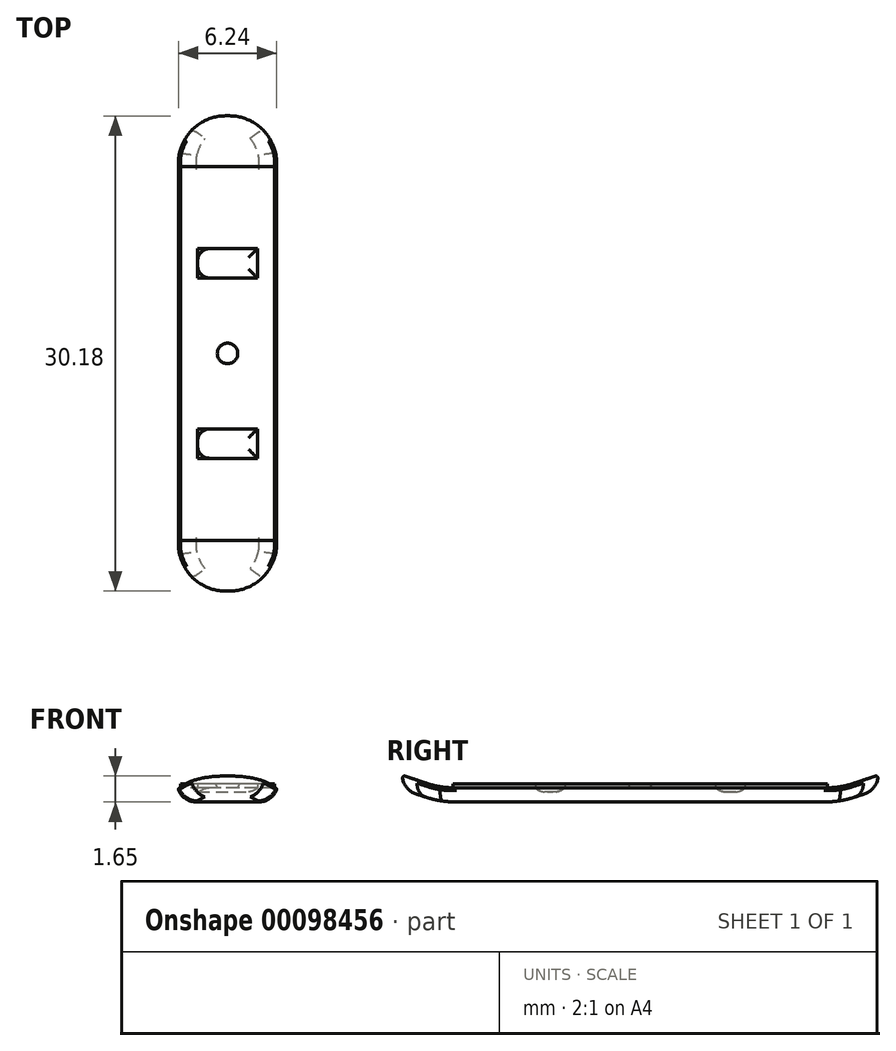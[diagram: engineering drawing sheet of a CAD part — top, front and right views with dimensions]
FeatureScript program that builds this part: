
annotation { "Feature Type Name" : "Feature", "Feature Type Description" : "" }
export const myFeature = defineFeature(function(context is Context, id is Id, definition is map)
    precondition{}
    {
        {
            var Q0;
            Q0=qCreatedBy(makeId("Right.planeOp"),FACE);
            var sketch = newSketch(context, id + "F0", { "sketchPlane" : qUnion([Q0])});
            skLineSegment(sketch, "E0", {"start": v(11.68, 0) * mm, "end": v(0, 0) * mm});
            skLineSegment(sketch, "E1", {"start": v(13.67, 0.32) * mm, "end": v(15.11, 0.8) * mm});
            skPoint(sketch, "E2.visualSharp", {"position": v(12.7, 0) * mm});
            skArc(sketch, "E2.filletArc", {"start": v(11.68, 0) * mm, "mid": v(12.69, 0.08) * mm, "end": v(13.67, 0.32) * mm});
            skLineSegment(sketch, "E3", {"start": v(0, 0.9) * mm, "end": v(12.7, 0.9) * mm});
            skLineSegment(sketch, "E4", {"start": v(12.7, 0.9) * mm, "end": v(15.11, 1.7) * mm});
            skLineSegment(sketch, "E5", {"start": v(15.11, 1.7) * mm, "end": v(15.11, 0.8) * mm});
            skLineSegment(sketch, "E6", {"start": v(0, 3.2) * mm, "end": v(0, -3.84) * mm});
            skLineSegment(sketch, "E7.MirrorCS", {"start": v(0, 0.9) * mm, "end": v(-12.7, 0.9) * mm});
            skLineSegment(sketch, "E8.MirrorCS", {"start": v(-11.68, 0) * mm, "end": v(0, 0) * mm});
            skArc(sketch, "E9.MirrorCS", {"start": v(-11.68, 0) * mm, "mid": v(-12.69, 0.08) * mm, "end": v(-13.67, 0.32) * mm});
            skLineSegment(sketch, "E10.MirrorCS", {"start": v(-12.7, 0.9) * mm, "end": v(-15.11, 1.7) * mm});
            skLineSegment(sketch, "E11.MirrorCS", {"start": v(-15.11, 1.7) * mm, "end": v(-15.11, 0.8) * mm});
            skLineSegment(sketch, "E12.MirrorCS", {"start": v(-13.67, 0.32) * mm, "end": v(-15.11, 0.8) * mm});
            skSolve(sketch);
        }
        {
            var Q0;
            {var subQ1=sQuery(id+"F0.wireOp",EDGE,"E7.MirrorCS");Q0=makeQuery(id+"F0.imprint","IMPRINT",FACE,{"disambiguationData":[TD([[makeQuery(id+"F0.imprint","IMPRINT",EDGE,{"derivedFrom":subQ1}),1.0]])]});}
            var Q1;
            {var subQ1=sQuery(id+"F0.wireOp",EDGE,"E0");Q1=makeQuery(id+"F0.imprint","IMPRINT",FACE,{"disambiguationData":[TD([[makeQuery(id+"F0.imprint","IMPRINT",EDGE,{"derivedFrom":subQ1}),-1.0]])]});}
            extrude(context, id + "F1", {"entities" : qUnion([Q0, Q1]), "depth" : 3.17 * mm});
        }
        {
            var Q0;
            Q0=makeQuery(id+"F1.opExtrude","CAP_FACE",FACE,{"disambiguationData":[OSD([sQuery(id+"F0.wireOp",EDGE,"E0"),sQuery(id+"F0.wireOp",EDGE,"E1"),sQuery(id+"F0.wireOp",EDGE,"E2.filletArc"),sQuery(id+"F0.wireOp",EDGE,"E3"),sQuery(id+"F0.wireOp",EDGE,"E4"),sQuery(id+"F0.wireOp",EDGE,"E5"),sQuery(id+"F0.wireOp",EDGE,"E7.MirrorCS"),sQuery(id+"F0.wireOp",EDGE,"E8.MirrorCS"),sQuery(id+"F0.wireOp",EDGE,"E9.MirrorCS"),sQuery(id+"F0.wireOp",EDGE,"E10.MirrorCS"),sQuery(id+"F0.wireOp",EDGE,"E11.MirrorCS"),sQuery(id+"F0.wireOp",EDGE,"E12.MirrorCS")])],"isStart":true});
            extrude(context, id + "F2", {"entities" : qUnion([Q0]), "operationType" : NewBodyOperationType.ADD, "depth" : 3.17 * mm});
        }
        {
            var Q0;
            Q0=makeQuery(id+"F1.opExtrude","CAP_EDGE",EDGE,{"disambiguationData":[OSD([sQuery(id+"F0.wireOp",EDGE,"E11.MirrorCS")])],"isStart":false});
            var Q1;
            Q1=makeQuery(id+"F2.opExtrude","CAP_EDGE",EDGE,{"disambiguationData":[OSD([sQuery(id+"F0.wireOp",EDGE,"E11.MirrorCS")])],"isStart":false});
            var Q2;
            Q2=makeQuery(id+"F1.opExtrude","CAP_EDGE",EDGE,{"disambiguationData":[OSD([sQuery(id+"F0.wireOp",EDGE,"E5")])],"isStart":false});
            var Q3;
            Q3=makeQuery(id+"F2.opExtrude","CAP_EDGE",EDGE,{"disambiguationData":[OSD([sQuery(id+"F0.wireOp",EDGE,"E5")])],"isStart":false});
            fillet(context, id + "F3", {"entities" : qUnion([Q0, Q1, Q2, Q3]), "radius" : 3.05 * mm, "tangentPropagation" : true, "allowEdgeOverflow" : false});
        }
        {
            var Q0;
            {var subQ0=sQuery(id+"F0.wireOp",EDGE,"E12.MirrorCS");Q0=makeQuery(id+"F3.opFillet","BLEND_EDGE",EDGE,{"blendedFrom":[makeQuery(id+"F2.opExtrude","CAP_EDGE",EDGE,{"disambiguationData":[OSD([sQuery(id+"F0.wireOp",EDGE,"E11.MirrorCS")])],"isStart":false}),makeQuery(id+"F2.boolean.opBoolean","MERGE",FACE,{"derivedFrom":[makeQuery(id+"F1.opExtrude","SWEPT_FACE",FACE,{"disambiguationData":[OSD([subQ0])]}),makeQuery(id+"F2.opExtrude","SWEPT_FACE",FACE,{"disambiguationData":[OSD([subQ0])]})]})],"blendedInto":[makeQuery(id+"F2.boolean.opBoolean","MERGE",FACE,{"derivedFrom":[makeQuery(id+"F1.opExtrude","SWEPT_FACE",FACE,{"disambiguationData":[OSD([subQ0])]}),makeQuery(id+"F2.opExtrude","SWEPT_FACE",FACE,{"disambiguationData":[OSD([subQ0])]})]})]});}
            var Q1;
            {var subQ0=sQuery(id+"F0.wireOp",EDGE,"E12.MirrorCS");Q1=makeQuery(id+"F3.opFillet","BLEND_EDGE",EDGE,{"blendedFrom":[makeQuery(id+"F1.opExtrude","CAP_EDGE",EDGE,{"disambiguationData":[OSD([sQuery(id+"F0.wireOp",EDGE,"E11.MirrorCS")])],"isStart":false}),makeQuery(id+"F2.boolean.opBoolean","MERGE",FACE,{"derivedFrom":[makeQuery(id+"F1.opExtrude","SWEPT_FACE",FACE,{"disambiguationData":[OSD([subQ0])]}),makeQuery(id+"F2.opExtrude","SWEPT_FACE",FACE,{"disambiguationData":[OSD([subQ0])]})]})],"blendedInto":[makeQuery(id+"F2.boolean.opBoolean","MERGE",FACE,{"derivedFrom":[makeQuery(id+"F1.opExtrude","SWEPT_FACE",FACE,{"disambiguationData":[OSD([subQ0])]}),makeQuery(id+"F2.opExtrude","SWEPT_FACE",FACE,{"disambiguationData":[OSD([subQ0])]})]})]});}
            var Q2;
            {var subQ0=sQuery(id+"F0.wireOp",EDGE,"E12.MirrorCS");var subQ1=sQuery(id+"F0.wireOp",EDGE,"E11.MirrorCS");Q2=makeQuery(id+"F2.boolean.opBoolean","MERGE",EDGE,{"derivedFrom":[makeQuery(id+"F1.opExtrude","SWEPT_EDGE",EDGE,{"disambiguationData":[OSD([subQ1,subQ0])]}),makeQuery(id+"F2.opExtrude","SWEPT_EDGE",EDGE,{"disambiguationData":[OSD([subQ1,subQ0])]})]});}
            var Q3;
            {var subQ0=sQuery(id+"F0.wireOp",EDGE,"E9.MirrorCS");Q3=makeQuery(id+"F3.opFillet","BLEND_EDGE",EDGE,{"blendedFrom":[makeQuery(id+"F1.opExtrude","CAP_EDGE",EDGE,{"disambiguationData":[OSD([sQuery(id+"F0.wireOp",EDGE,"E11.MirrorCS")])],"isStart":false}),makeQuery(id+"F2.boolean.opBoolean","MERGE",FACE,{"derivedFrom":[makeQuery(id+"F1.opExtrude","SWEPT_FACE",FACE,{"disambiguationData":[OSD([subQ0])]}),makeQuery(id+"F2.opExtrude","SWEPT_FACE",FACE,{"disambiguationData":[OSD([subQ0])]})]})],"blendedInto":[makeQuery(id+"F2.boolean.opBoolean","MERGE",FACE,{"derivedFrom":[makeQuery(id+"F1.opExtrude","SWEPT_FACE",FACE,{"disambiguationData":[OSD([subQ0])]}),makeQuery(id+"F2.opExtrude","SWEPT_FACE",FACE,{"disambiguationData":[OSD([subQ0])]})]})]});}
            var Q4;
            {var subQ0=sQuery(id+"F0.wireOp",EDGE,"E9.MirrorCS");Q4=makeQuery(id+"F3.opFillet","BLEND_EDGE",EDGE,{"blendedFrom":[makeQuery(id+"F2.opExtrude","CAP_EDGE",EDGE,{"disambiguationData":[OSD([sQuery(id+"F0.wireOp",EDGE,"E11.MirrorCS")])],"isStart":false}),makeQuery(id+"F2.boolean.opBoolean","MERGE",FACE,{"derivedFrom":[makeQuery(id+"F1.opExtrude","SWEPT_FACE",FACE,{"disambiguationData":[OSD([subQ0])]}),makeQuery(id+"F2.opExtrude","SWEPT_FACE",FACE,{"disambiguationData":[OSD([subQ0])]})]})],"blendedInto":[makeQuery(id+"F2.boolean.opBoolean","MERGE",FACE,{"derivedFrom":[makeQuery(id+"F1.opExtrude","SWEPT_FACE",FACE,{"disambiguationData":[OSD([subQ0])]}),makeQuery(id+"F2.opExtrude","SWEPT_FACE",FACE,{"disambiguationData":[OSD([subQ0])]})]})]});}
            fillet(context, id + "F4", {"entities" : qUnion([Q0, Q1, Q2, Q3, Q4]), "radius" : 1.27 * mm, "tangentPropagation" : true, "allowEdgeOverflow" : false});
        }
        {
            var Q0;
            {var subQ0=sQuery(id+"F0.wireOp",EDGE,"E4");var subQ1=sQuery(id+"F0.wireOp",EDGE,"E3");Q0=makeQuery(id+"F2.boolean.opBoolean","MERGE",EDGE,{"derivedFrom":[makeQuery(id+"F1.opExtrude","SWEPT_EDGE",EDGE,{"disambiguationData":[OSD([subQ1,subQ0])]}),makeQuery(id+"F2.opExtrude","SWEPT_EDGE",EDGE,{"disambiguationData":[OSD([subQ1,subQ0])]})]});}
            var Q1;
            {var subQ0=sQuery(id+"F0.wireOp",EDGE,"E10.MirrorCS");var subQ1=sQuery(id+"F0.wireOp",EDGE,"E7.MirrorCS");Q1=makeQuery(id+"F2.boolean.opBoolean","MERGE",EDGE,{"derivedFrom":[makeQuery(id+"F1.opExtrude","SWEPT_EDGE",EDGE,{"disambiguationData":[OSD([subQ1,subQ0])]}),makeQuery(id+"F2.opExtrude","SWEPT_EDGE",EDGE,{"disambiguationData":[OSD([subQ1,subQ0])]})]});}
            fillet(context, id + "F5", {"entities" : qUnion([Q0, Q1]), "radius" : 5.08 * mm, "tangentPropagation" : true, "allowEdgeOverflow" : false});
        }
        {
            var Q0;
            {var subQ0=sQuery(id+"F0.wireOp",EDGE,"E7.MirrorCS");var subQ1=sQuery(id+"F0.wireOp",EDGE,"E3");Q0=makeQuery(id+"F4.opFillet","BLEND_EDGE",EDGE,{"disambiguationData":[OD(1.0)],"blendedFrom":[makeQuery(id+"F1.opExtrude","CAP_EDGE",EDGE,{"disambiguationData":[OSD([sQuery(id+"F0.wireOp",EDGE,"E2.filletArc")])],"isStart":false}),makeQuery(id+"F2.boolean.opBoolean","MERGE",FACE,{"derivedFrom":[makeQuery(id+"F1.opExtrude","SWEPT_FACE",FACE,{"disambiguationData":[OSD([subQ1,subQ0])]}),makeQuery(id+"F2.opExtrude","SWEPT_FACE",FACE,{"disambiguationData":[OSD([subQ1,subQ0])]})]})],"blendedInto":[makeQuery(id+"F2.boolean.opBoolean","MERGE",FACE,{"derivedFrom":[makeQuery(id+"F1.opExtrude","SWEPT_FACE",FACE,{"disambiguationData":[OSD([subQ1,subQ0])]}),makeQuery(id+"F2.opExtrude","SWEPT_FACE",FACE,{"disambiguationData":[OSD([subQ1,subQ0])]})]})]});}
            var Q1;
            {var subQ0=sQuery(id+"F0.wireOp",EDGE,"E7.MirrorCS");var subQ1=sQuery(id+"F0.wireOp",EDGE,"E3");Q1=makeQuery(id+"F4.opFillet","BLEND_EDGE",EDGE,{"disambiguationData":[OD(1.0)],"blendedFrom":[makeQuery(id+"F2.opExtrude","CAP_EDGE",EDGE,{"disambiguationData":[OSD([sQuery(id+"F0.wireOp",EDGE,"E9.MirrorCS")])],"isStart":false}),makeQuery(id+"F2.boolean.opBoolean","MERGE",FACE,{"derivedFrom":[makeQuery(id+"F1.opExtrude","SWEPT_FACE",FACE,{"disambiguationData":[OSD([subQ1,subQ0])]}),makeQuery(id+"F2.opExtrude","SWEPT_FACE",FACE,{"disambiguationData":[OSD([subQ1,subQ0])]})]})],"blendedInto":[makeQuery(id+"F2.boolean.opBoolean","MERGE",FACE,{"derivedFrom":[makeQuery(id+"F1.opExtrude","SWEPT_FACE",FACE,{"disambiguationData":[OSD([subQ1,subQ0])]}),makeQuery(id+"F2.opExtrude","SWEPT_FACE",FACE,{"disambiguationData":[OSD([subQ1,subQ0])]})]})]});}
            var Q2;
            {var subQ0=sQuery(id+"F0.wireOp",EDGE,"E7.MirrorCS");var subQ1=sQuery(id+"F0.wireOp",EDGE,"E3");Q2=makeQuery(id+"F4.opFillet","BLEND_EDGE",EDGE,{"disambiguationData":[OD(0.0)],"blendedFrom":[makeQuery(id+"F2.opExtrude","CAP_EDGE",EDGE,{"disambiguationData":[OSD([sQuery(id+"F0.wireOp",EDGE,"E9.MirrorCS")])],"isStart":false}),makeQuery(id+"F2.boolean.opBoolean","MERGE",FACE,{"derivedFrom":[makeQuery(id+"F1.opExtrude","SWEPT_FACE",FACE,{"disambiguationData":[OSD([subQ1,subQ0])]}),makeQuery(id+"F2.opExtrude","SWEPT_FACE",FACE,{"disambiguationData":[OSD([subQ1,subQ0])]})]})],"blendedInto":[makeQuery(id+"F2.boolean.opBoolean","MERGE",FACE,{"derivedFrom":[makeQuery(id+"F1.opExtrude","SWEPT_FACE",FACE,{"disambiguationData":[OSD([subQ1,subQ0])]}),makeQuery(id+"F2.opExtrude","SWEPT_FACE",FACE,{"disambiguationData":[OSD([subQ1,subQ0])]})]})]});}
            var Q3;
            {var subQ0=sQuery(id+"F0.wireOp",EDGE,"E9.MirrorCS");var subQ1=sQuery(id+"F0.wireOp",EDGE,"E10.MirrorCS");var subQ2=sQuery(id+"F0.wireOp",EDGE,"E7.MirrorCS");Q3=makeQuery(id+"F5.opFillet","BLEND_EDGE",EDGE,{"blendedFrom":[makeQuery(id+"F2.boolean.opBoolean","MERGE",EDGE,{"derivedFrom":[makeQuery(id+"F1.opExtrude","SWEPT_EDGE",EDGE,{"disambiguationData":[OSD([subQ2,subQ1])]}),makeQuery(id+"F2.opExtrude","SWEPT_EDGE",EDGE,{"disambiguationData":[OSD([subQ2,subQ1])]})]}),makeQuery(id+"F4.opFillet","BLEND_FACE",FACE,{"disambiguationData":[OSD([subQ0]),TDD([makeQuery(id+"F2.opExtrude","CAP_EDGE",EDGE,{"disambiguationData":[OSD([subQ0])],"isStart":false})]),OD(1.0)]})],"blendedInto":[makeQuery(id+"F4.opFillet","BLEND_FACE",FACE,{"disambiguationData":[OSD([subQ0]),TDD([makeQuery(id+"F2.opExtrude","CAP_EDGE",EDGE,{"disambiguationData":[OSD([subQ0])],"isStart":false})]),OD(1.0)]})]});}
            var Q4;
            {var subQ0=sQuery(id+"F0.wireOp",EDGE,"E9.MirrorCS");var subQ1=sQuery(id+"F0.wireOp",EDGE,"E11.MirrorCS");var subQ2=sQuery(id+"F0.wireOp",EDGE,"E10.MirrorCS");var subQ3=sQuery(id+"F0.wireOp",EDGE,"E7.MirrorCS");Q4=makeQuery(id+"F5.opFillet","BLEND_EDGE",EDGE,{"blendedFrom":[makeQuery(id+"F2.boolean.opBoolean","MERGE",EDGE,{"derivedFrom":[makeQuery(id+"F1.opExtrude","SWEPT_EDGE",EDGE,{"disambiguationData":[OSD([subQ3,subQ2])]}),makeQuery(id+"F2.opExtrude","SWEPT_EDGE",EDGE,{"disambiguationData":[OSD([subQ3,subQ2])]})]}),makeQuery(id+"F4.opFillet","BLEND_FACE",FACE,{"disambiguationData":[OSD([subQ0,subQ1]),TDD([makeQuery(id+"F3.opFillet","BLEND_EDGE",EDGE,{"blendedFrom":[makeQuery(id+"F2.opExtrude","CAP_EDGE",EDGE,{"disambiguationData":[OSD([subQ1])],"isStart":false}),makeQuery(id+"F2.boolean.opBoolean","MERGE",FACE,{"derivedFrom":[makeQuery(id+"F1.opExtrude","SWEPT_FACE",FACE,{"disambiguationData":[OSD([subQ0])]}),makeQuery(id+"F2.opExtrude","SWEPT_FACE",FACE,{"disambiguationData":[OSD([subQ0])]})]})],"blendedInto":[makeQuery(id+"F2.boolean.opBoolean","MERGE",FACE,{"derivedFrom":[makeQuery(id+"F1.opExtrude","SWEPT_FACE",FACE,{"disambiguationData":[OSD([subQ0])]}),makeQuery(id+"F2.opExtrude","SWEPT_FACE",FACE,{"disambiguationData":[OSD([subQ0])]})]})]})])]})],"blendedInto":[makeQuery(id+"F4.opFillet","BLEND_FACE",FACE,{"disambiguationData":[OSD([subQ0,subQ1]),TDD([makeQuery(id+"F3.opFillet","BLEND_EDGE",EDGE,{"blendedFrom":[makeQuery(id+"F2.opExtrude","CAP_EDGE",EDGE,{"disambiguationData":[OSD([subQ1])],"isStart":false}),makeQuery(id+"F2.boolean.opBoolean","MERGE",FACE,{"derivedFrom":[makeQuery(id+"F1.opExtrude","SWEPT_FACE",FACE,{"disambiguationData":[OSD([subQ0])]}),makeQuery(id+"F2.opExtrude","SWEPT_FACE",FACE,{"disambiguationData":[OSD([subQ0])]})]})],"blendedInto":[makeQuery(id+"F2.boolean.opBoolean","MERGE",FACE,{"derivedFrom":[makeQuery(id+"F1.opExtrude","SWEPT_FACE",FACE,{"disambiguationData":[OSD([subQ0])]}),makeQuery(id+"F2.opExtrude","SWEPT_FACE",FACE,{"disambiguationData":[OSD([subQ0])]})]})]})])]})]});}
            var Q5;
            {var subQ0=sQuery(id+"F0.wireOp",EDGE,"E12.MirrorCS");var subQ1=sQuery(id+"F0.wireOp",EDGE,"E11.MirrorCS");var subQ2=sQuery(id+"F0.wireOp",EDGE,"E10.MirrorCS");var subQ3=sQuery(id+"F0.wireOp",EDGE,"E7.MirrorCS");Q5=makeQuery(id+"F5.opFillet","BLEND_EDGE",EDGE,{"blendedFrom":[makeQuery(id+"F2.boolean.opBoolean","MERGE",EDGE,{"derivedFrom":[makeQuery(id+"F1.opExtrude","SWEPT_EDGE",EDGE,{"disambiguationData":[OSD([subQ3,subQ2])]}),makeQuery(id+"F2.opExtrude","SWEPT_EDGE",EDGE,{"disambiguationData":[OSD([subQ3,subQ2])]})]}),makeQuery(id+"F4.opFillet","BLEND_FACE",FACE,{"disambiguationData":[OSD([subQ1,subQ0]),TDD([makeQuery(id+"F3.opFillet","BLEND_EDGE",EDGE,{"blendedFrom":[makeQuery(id+"F2.opExtrude","CAP_EDGE",EDGE,{"disambiguationData":[OSD([subQ1])],"isStart":false}),makeQuery(id+"F2.boolean.opBoolean","MERGE",FACE,{"derivedFrom":[makeQuery(id+"F1.opExtrude","SWEPT_FACE",FACE,{"disambiguationData":[OSD([subQ0])]}),makeQuery(id+"F2.opExtrude","SWEPT_FACE",FACE,{"disambiguationData":[OSD([subQ0])]})]})],"blendedInto":[makeQuery(id+"F2.boolean.opBoolean","MERGE",FACE,{"derivedFrom":[makeQuery(id+"F1.opExtrude","SWEPT_FACE",FACE,{"disambiguationData":[OSD([subQ0])]}),makeQuery(id+"F2.opExtrude","SWEPT_FACE",FACE,{"disambiguationData":[OSD([subQ0])]})]})]})]),OD(0.0)]})],"blendedInto":[makeQuery(id+"F4.opFillet","BLEND_FACE",FACE,{"disambiguationData":[OSD([subQ1,subQ0]),TDD([makeQuery(id+"F3.opFillet","BLEND_EDGE",EDGE,{"blendedFrom":[makeQuery(id+"F2.opExtrude","CAP_EDGE",EDGE,{"disambiguationData":[OSD([subQ1])],"isStart":false}),makeQuery(id+"F2.boolean.opBoolean","MERGE",FACE,{"derivedFrom":[makeQuery(id+"F1.opExtrude","SWEPT_FACE",FACE,{"disambiguationData":[OSD([subQ0])]}),makeQuery(id+"F2.opExtrude","SWEPT_FACE",FACE,{"disambiguationData":[OSD([subQ0])]})]})],"blendedInto":[makeQuery(id+"F2.boolean.opBoolean","MERGE",FACE,{"derivedFrom":[makeQuery(id+"F1.opExtrude","SWEPT_FACE",FACE,{"disambiguationData":[OSD([subQ0])]}),makeQuery(id+"F2.opExtrude","SWEPT_FACE",FACE,{"disambiguationData":[OSD([subQ0])]})]})]})]),OD(0.0)]})]});}
            var Q6;
            {var subQ0=sQuery(id+"F0.wireOp",EDGE,"E10.MirrorCS");var subQ1=sQuery(id+"F0.wireOp",EDGE,"E12.MirrorCS");Q6=makeQuery(id+"F4.opFillet","BLEND_EDGE",EDGE,{"disambiguationData":[OD(0.0)],"blendedFrom":[makeQuery(id+"F3.opFillet","BLEND_EDGE",EDGE,{"blendedFrom":[makeQuery(id+"F2.opExtrude","CAP_EDGE",EDGE,{"disambiguationData":[OSD([sQuery(id+"F0.wireOp",EDGE,"E11.MirrorCS")])],"isStart":false}),makeQuery(id+"F2.boolean.opBoolean","MERGE",FACE,{"derivedFrom":[makeQuery(id+"F1.opExtrude","SWEPT_FACE",FACE,{"disambiguationData":[OSD([subQ1])]}),makeQuery(id+"F2.opExtrude","SWEPT_FACE",FACE,{"disambiguationData":[OSD([subQ1])]})]})],"blendedInto":[makeQuery(id+"F2.boolean.opBoolean","MERGE",FACE,{"derivedFrom":[makeQuery(id+"F1.opExtrude","SWEPT_FACE",FACE,{"disambiguationData":[OSD([subQ1])]}),makeQuery(id+"F2.opExtrude","SWEPT_FACE",FACE,{"disambiguationData":[OSD([subQ1])]})]})]}),makeQuery(id+"F2.boolean.opBoolean","MERGE",FACE,{"derivedFrom":[makeQuery(id+"F1.opExtrude","SWEPT_FACE",FACE,{"disambiguationData":[OSD([subQ0])]}),makeQuery(id+"F2.opExtrude","SWEPT_FACE",FACE,{"disambiguationData":[OSD([subQ0])]})]})],"blendedInto":[makeQuery(id+"F2.boolean.opBoolean","MERGE",FACE,{"derivedFrom":[makeQuery(id+"F1.opExtrude","SWEPT_FACE",FACE,{"disambiguationData":[OSD([subQ0])]}),makeQuery(id+"F2.opExtrude","SWEPT_FACE",FACE,{"disambiguationData":[OSD([subQ0])]})]})]});}
            var Q7;
            {var subQ0=sQuery(id+"F0.wireOp",EDGE,"E10.MirrorCS");var subQ1=sQuery(id+"F0.wireOp",EDGE,"E12.MirrorCS");Q7=makeQuery(id+"F4.opFillet","BLEND_EDGE",EDGE,{"disambiguationData":[OD(1.0)],"blendedFrom":[makeQuery(id+"F3.opFillet","BLEND_EDGE",EDGE,{"blendedFrom":[makeQuery(id+"F2.opExtrude","CAP_EDGE",EDGE,{"disambiguationData":[OSD([sQuery(id+"F0.wireOp",EDGE,"E11.MirrorCS")])],"isStart":false}),makeQuery(id+"F2.boolean.opBoolean","MERGE",FACE,{"derivedFrom":[makeQuery(id+"F1.opExtrude","SWEPT_FACE",FACE,{"disambiguationData":[OSD([subQ1])]}),makeQuery(id+"F2.opExtrude","SWEPT_FACE",FACE,{"disambiguationData":[OSD([subQ1])]})]})],"blendedInto":[makeQuery(id+"F2.boolean.opBoolean","MERGE",FACE,{"derivedFrom":[makeQuery(id+"F1.opExtrude","SWEPT_FACE",FACE,{"disambiguationData":[OSD([subQ1])]}),makeQuery(id+"F2.opExtrude","SWEPT_FACE",FACE,{"disambiguationData":[OSD([subQ1])]})]})]}),makeQuery(id+"F2.boolean.opBoolean","MERGE",FACE,{"derivedFrom":[makeQuery(id+"F1.opExtrude","SWEPT_FACE",FACE,{"disambiguationData":[OSD([subQ0])]}),makeQuery(id+"F2.opExtrude","SWEPT_FACE",FACE,{"disambiguationData":[OSD([subQ0])]})]})],"blendedInto":[makeQuery(id+"F2.boolean.opBoolean","MERGE",FACE,{"derivedFrom":[makeQuery(id+"F1.opExtrude","SWEPT_FACE",FACE,{"disambiguationData":[OSD([subQ0])]}),makeQuery(id+"F2.opExtrude","SWEPT_FACE",FACE,{"disambiguationData":[OSD([subQ0])]})]})]});}
            var Q8;
            {var subQ0=sQuery(id+"F0.wireOp",EDGE,"E10.MirrorCS");var subQ1=sQuery(id+"F0.wireOp",EDGE,"E12.MirrorCS");var subQ2=sQuery(id+"F0.wireOp",EDGE,"E11.MirrorCS");Q8=makeQuery(id+"F4.opFillet","BLEND_EDGE",EDGE,{"blendedFrom":[makeQuery(id+"F2.boolean.opBoolean","MERGE",EDGE,{"derivedFrom":[makeQuery(id+"F1.opExtrude","SWEPT_EDGE",EDGE,{"disambiguationData":[OSD([subQ2,subQ1])]}),makeQuery(id+"F2.opExtrude","SWEPT_EDGE",EDGE,{"disambiguationData":[OSD([subQ2,subQ1])]})]}),makeQuery(id+"F2.boolean.opBoolean","MERGE",FACE,{"derivedFrom":[makeQuery(id+"F1.opExtrude","SWEPT_FACE",FACE,{"disambiguationData":[OSD([subQ0])]}),makeQuery(id+"F2.opExtrude","SWEPT_FACE",FACE,{"disambiguationData":[OSD([subQ0])]})]})],"blendedInto":[makeQuery(id+"F2.boolean.opBoolean","MERGE",FACE,{"derivedFrom":[makeQuery(id+"F1.opExtrude","SWEPT_FACE",FACE,{"disambiguationData":[OSD([subQ0])]}),makeQuery(id+"F2.opExtrude","SWEPT_FACE",FACE,{"disambiguationData":[OSD([subQ0])]})]})]});}
            var Q9;
            {var subQ0=sQuery(id+"F0.wireOp",EDGE,"E10.MirrorCS");var subQ1=sQuery(id+"F0.wireOp",EDGE,"E12.MirrorCS");Q9=makeQuery(id+"F4.opFillet","BLEND_EDGE",EDGE,{"blendedFrom":[makeQuery(id+"F3.opFillet","BLEND_EDGE",EDGE,{"blendedFrom":[makeQuery(id+"F1.opExtrude","CAP_EDGE",EDGE,{"disambiguationData":[OSD([sQuery(id+"F0.wireOp",EDGE,"E11.MirrorCS")])],"isStart":false}),makeQuery(id+"F2.boolean.opBoolean","MERGE",FACE,{"derivedFrom":[makeQuery(id+"F1.opExtrude","SWEPT_FACE",FACE,{"disambiguationData":[OSD([subQ1])]}),makeQuery(id+"F2.opExtrude","SWEPT_FACE",FACE,{"disambiguationData":[OSD([subQ1])]})]})],"blendedInto":[makeQuery(id+"F2.boolean.opBoolean","MERGE",FACE,{"derivedFrom":[makeQuery(id+"F1.opExtrude","SWEPT_FACE",FACE,{"disambiguationData":[OSD([subQ1])]}),makeQuery(id+"F2.opExtrude","SWEPT_FACE",FACE,{"disambiguationData":[OSD([subQ1])]})]})]}),makeQuery(id+"F2.boolean.opBoolean","MERGE",FACE,{"derivedFrom":[makeQuery(id+"F1.opExtrude","SWEPT_FACE",FACE,{"disambiguationData":[OSD([subQ0])]}),makeQuery(id+"F2.opExtrude","SWEPT_FACE",FACE,{"disambiguationData":[OSD([subQ0])]})]})],"blendedInto":[makeQuery(id+"F2.boolean.opBoolean","MERGE",FACE,{"derivedFrom":[makeQuery(id+"F1.opExtrude","SWEPT_FACE",FACE,{"disambiguationData":[OSD([subQ0])]}),makeQuery(id+"F2.opExtrude","SWEPT_FACE",FACE,{"disambiguationData":[OSD([subQ0])]})]})]});}
            var Q10;
            {var subQ0=sQuery(id+"F0.wireOp",EDGE,"E10.MirrorCS");var subQ1=sQuery(id+"F0.wireOp",EDGE,"E9.MirrorCS");Q10=makeQuery(id+"F4.opFillet","BLEND_EDGE",EDGE,{"blendedFrom":[makeQuery(id+"F3.opFillet","BLEND_EDGE",EDGE,{"blendedFrom":[makeQuery(id+"F1.opExtrude","CAP_EDGE",EDGE,{"disambiguationData":[OSD([sQuery(id+"F0.wireOp",EDGE,"E11.MirrorCS")])],"isStart":false}),makeQuery(id+"F2.boolean.opBoolean","MERGE",FACE,{"derivedFrom":[makeQuery(id+"F1.opExtrude","SWEPT_FACE",FACE,{"disambiguationData":[OSD([subQ1])]}),makeQuery(id+"F2.opExtrude","SWEPT_FACE",FACE,{"disambiguationData":[OSD([subQ1])]})]})],"blendedInto":[makeQuery(id+"F2.boolean.opBoolean","MERGE",FACE,{"derivedFrom":[makeQuery(id+"F1.opExtrude","SWEPT_FACE",FACE,{"disambiguationData":[OSD([subQ1])]}),makeQuery(id+"F2.opExtrude","SWEPT_FACE",FACE,{"disambiguationData":[OSD([subQ1])]})]})]}),makeQuery(id+"F2.boolean.opBoolean","MERGE",FACE,{"derivedFrom":[makeQuery(id+"F1.opExtrude","SWEPT_FACE",FACE,{"disambiguationData":[OSD([subQ0])]}),makeQuery(id+"F2.opExtrude","SWEPT_FACE",FACE,{"disambiguationData":[OSD([subQ0])]})]})],"blendedInto":[makeQuery(id+"F2.boolean.opBoolean","MERGE",FACE,{"derivedFrom":[makeQuery(id+"F1.opExtrude","SWEPT_FACE",FACE,{"disambiguationData":[OSD([subQ0])]}),makeQuery(id+"F2.opExtrude","SWEPT_FACE",FACE,{"disambiguationData":[OSD([subQ0])]})]})]});}
            var Q11;
            {var subQ0=sQuery(id+"F0.wireOp",EDGE,"E9.MirrorCS");var subQ1=sQuery(id+"F0.wireOp",EDGE,"E11.MirrorCS");var subQ2=sQuery(id+"F0.wireOp",EDGE,"E10.MirrorCS");var subQ3=sQuery(id+"F0.wireOp",EDGE,"E7.MirrorCS");Q11=makeQuery(id+"F5.opFillet","BLEND_EDGE",EDGE,{"blendedFrom":[makeQuery(id+"F2.boolean.opBoolean","MERGE",EDGE,{"derivedFrom":[makeQuery(id+"F1.opExtrude","SWEPT_EDGE",EDGE,{"disambiguationData":[OSD([subQ3,subQ2])]}),makeQuery(id+"F2.opExtrude","SWEPT_EDGE",EDGE,{"disambiguationData":[OSD([subQ3,subQ2])]})]}),makeQuery(id+"F4.opFillet","BLEND_FACE",FACE,{"disambiguationData":[OSD([subQ0,subQ1]),TDD([makeQuery(id+"F3.opFillet","BLEND_EDGE",EDGE,{"blendedFrom":[makeQuery(id+"F1.opExtrude","CAP_EDGE",EDGE,{"disambiguationData":[OSD([subQ1])],"isStart":false}),makeQuery(id+"F2.boolean.opBoolean","MERGE",FACE,{"derivedFrom":[makeQuery(id+"F1.opExtrude","SWEPT_FACE",FACE,{"disambiguationData":[OSD([subQ0])]}),makeQuery(id+"F2.opExtrude","SWEPT_FACE",FACE,{"disambiguationData":[OSD([subQ0])]})]})],"blendedInto":[makeQuery(id+"F2.boolean.opBoolean","MERGE",FACE,{"derivedFrom":[makeQuery(id+"F1.opExtrude","SWEPT_FACE",FACE,{"disambiguationData":[OSD([subQ0])]}),makeQuery(id+"F2.opExtrude","SWEPT_FACE",FACE,{"disambiguationData":[OSD([subQ0])]})]})]})]),OD(0.0)]})],"blendedInto":[makeQuery(id+"F4.opFillet","BLEND_FACE",FACE,{"disambiguationData":[OSD([subQ0,subQ1]),TDD([makeQuery(id+"F3.opFillet","BLEND_EDGE",EDGE,{"blendedFrom":[makeQuery(id+"F1.opExtrude","CAP_EDGE",EDGE,{"disambiguationData":[OSD([subQ1])],"isStart":false}),makeQuery(id+"F2.boolean.opBoolean","MERGE",FACE,{"derivedFrom":[makeQuery(id+"F1.opExtrude","SWEPT_FACE",FACE,{"disambiguationData":[OSD([subQ0])]}),makeQuery(id+"F2.opExtrude","SWEPT_FACE",FACE,{"disambiguationData":[OSD([subQ0])]})]})],"blendedInto":[makeQuery(id+"F2.boolean.opBoolean","MERGE",FACE,{"derivedFrom":[makeQuery(id+"F1.opExtrude","SWEPT_FACE",FACE,{"disambiguationData":[OSD([subQ0])]}),makeQuery(id+"F2.opExtrude","SWEPT_FACE",FACE,{"disambiguationData":[OSD([subQ0])]})]})]})]),OD(0.0)]})]});}
            var Q12;
            {var subQ0=sQuery(id+"F0.wireOp",EDGE,"E9.MirrorCS");var subQ1=sQuery(id+"F0.wireOp",EDGE,"E11.MirrorCS");var subQ2=sQuery(id+"F0.wireOp",EDGE,"E10.MirrorCS");var subQ3=sQuery(id+"F0.wireOp",EDGE,"E7.MirrorCS");Q12=makeQuery(id+"F5.opFillet","BLEND_EDGE",EDGE,{"blendedFrom":[makeQuery(id+"F2.boolean.opBoolean","MERGE",EDGE,{"derivedFrom":[makeQuery(id+"F1.opExtrude","SWEPT_EDGE",EDGE,{"disambiguationData":[OSD([subQ3,subQ2])]}),makeQuery(id+"F2.opExtrude","SWEPT_EDGE",EDGE,{"disambiguationData":[OSD([subQ3,subQ2])]})]}),makeQuery(id+"F4.opFillet","BLEND_FACE",FACE,{"disambiguationData":[OSD([subQ0,subQ1]),TDD([makeQuery(id+"F3.opFillet","BLEND_EDGE",EDGE,{"blendedFrom":[makeQuery(id+"F1.opExtrude","CAP_EDGE",EDGE,{"disambiguationData":[OSD([subQ1])],"isStart":false}),makeQuery(id+"F2.boolean.opBoolean","MERGE",FACE,{"derivedFrom":[makeQuery(id+"F1.opExtrude","SWEPT_FACE",FACE,{"disambiguationData":[OSD([subQ0])]}),makeQuery(id+"F2.opExtrude","SWEPT_FACE",FACE,{"disambiguationData":[OSD([subQ0])]})]})],"blendedInto":[makeQuery(id+"F2.boolean.opBoolean","MERGE",FACE,{"derivedFrom":[makeQuery(id+"F1.opExtrude","SWEPT_FACE",FACE,{"disambiguationData":[OSD([subQ0])]}),makeQuery(id+"F2.opExtrude","SWEPT_FACE",FACE,{"disambiguationData":[OSD([subQ0])]})]})]})]),OD(1.0)]})],"blendedInto":[makeQuery(id+"F4.opFillet","BLEND_FACE",FACE,{"disambiguationData":[OSD([subQ0,subQ1]),TDD([makeQuery(id+"F3.opFillet","BLEND_EDGE",EDGE,{"blendedFrom":[makeQuery(id+"F1.opExtrude","CAP_EDGE",EDGE,{"disambiguationData":[OSD([subQ1])],"isStart":false}),makeQuery(id+"F2.boolean.opBoolean","MERGE",FACE,{"derivedFrom":[makeQuery(id+"F1.opExtrude","SWEPT_FACE",FACE,{"disambiguationData":[OSD([subQ0])]}),makeQuery(id+"F2.opExtrude","SWEPT_FACE",FACE,{"disambiguationData":[OSD([subQ0])]})]})],"blendedInto":[makeQuery(id+"F2.boolean.opBoolean","MERGE",FACE,{"derivedFrom":[makeQuery(id+"F1.opExtrude","SWEPT_FACE",FACE,{"disambiguationData":[OSD([subQ0])]}),makeQuery(id+"F2.opExtrude","SWEPT_FACE",FACE,{"disambiguationData":[OSD([subQ0])]})]})]})]),OD(1.0)]})]});}
            var Q13;
            {var subQ0=sQuery(id+"F0.wireOp",EDGE,"E7.MirrorCS");var subQ1=sQuery(id+"F0.wireOp",EDGE,"E3");Q13=makeQuery(id+"F4.opFillet","BLEND_EDGE",EDGE,{"blendedFrom":[makeQuery(id+"F1.opExtrude","CAP_EDGE",EDGE,{"disambiguationData":[OSD([sQuery(id+"F0.wireOp",EDGE,"E9.MirrorCS")])],"isStart":false}),makeQuery(id+"F2.boolean.opBoolean","MERGE",FACE,{"derivedFrom":[makeQuery(id+"F1.opExtrude","SWEPT_FACE",FACE,{"disambiguationData":[OSD([subQ1,subQ0])]}),makeQuery(id+"F2.opExtrude","SWEPT_FACE",FACE,{"disambiguationData":[OSD([subQ1,subQ0])]})]})],"blendedInto":[makeQuery(id+"F2.boolean.opBoolean","MERGE",FACE,{"derivedFrom":[makeQuery(id+"F1.opExtrude","SWEPT_FACE",FACE,{"disambiguationData":[OSD([subQ1,subQ0])]}),makeQuery(id+"F2.opExtrude","SWEPT_FACE",FACE,{"disambiguationData":[OSD([subQ1,subQ0])]})]})]});}
            var Q14;
            {var subQ0=sQuery(id+"F0.wireOp",EDGE,"E9.MirrorCS");var subQ1=sQuery(id+"F0.wireOp",EDGE,"E10.MirrorCS");var subQ2=sQuery(id+"F0.wireOp",EDGE,"E7.MirrorCS");Q14=makeQuery(id+"F5.opFillet","BLEND_EDGE",EDGE,{"blendedFrom":[makeQuery(id+"F2.boolean.opBoolean","MERGE",EDGE,{"derivedFrom":[makeQuery(id+"F1.opExtrude","SWEPT_EDGE",EDGE,{"disambiguationData":[OSD([subQ2,subQ1])]}),makeQuery(id+"F2.opExtrude","SWEPT_EDGE",EDGE,{"disambiguationData":[OSD([subQ2,subQ1])]})]}),makeQuery(id+"F4.opFillet","BLEND_FACE",FACE,{"disambiguationData":[OSD([subQ0]),TDD([makeQuery(id+"F1.opExtrude","CAP_EDGE",EDGE,{"disambiguationData":[OSD([subQ0])],"isStart":false})])]})],"blendedInto":[makeQuery(id+"F4.opFillet","BLEND_FACE",FACE,{"disambiguationData":[OSD([subQ0]),TDD([makeQuery(id+"F1.opExtrude","CAP_EDGE",EDGE,{"disambiguationData":[OSD([subQ0])],"isStart":false})])]})]});}
            var Q15;
            {var subQ0=sQuery(id+"F0.wireOp",EDGE,"E7.MirrorCS");var subQ1=sQuery(id+"F0.wireOp",EDGE,"E3");Q15=makeQuery(id+"F4.opFillet","BLEND_EDGE",EDGE,{"disambiguationData":[OD(0.0)],"blendedFrom":[makeQuery(id+"F1.opExtrude","CAP_EDGE",EDGE,{"disambiguationData":[OSD([sQuery(id+"F0.wireOp",EDGE,"E2.filletArc")])],"isStart":false}),makeQuery(id+"F2.boolean.opBoolean","MERGE",FACE,{"derivedFrom":[makeQuery(id+"F1.opExtrude","SWEPT_FACE",FACE,{"disambiguationData":[OSD([subQ1,subQ0])]}),makeQuery(id+"F2.opExtrude","SWEPT_FACE",FACE,{"disambiguationData":[OSD([subQ1,subQ0])]})]})],"blendedInto":[makeQuery(id+"F2.boolean.opBoolean","MERGE",FACE,{"derivedFrom":[makeQuery(id+"F1.opExtrude","SWEPT_FACE",FACE,{"disambiguationData":[OSD([subQ1,subQ0])]}),makeQuery(id+"F2.opExtrude","SWEPT_FACE",FACE,{"disambiguationData":[OSD([subQ1,subQ0])]})]})]});}
            var Q16;
            {var subQ0=sQuery(id+"F0.wireOp",EDGE,"E2.filletArc");var subQ1=sQuery(id+"F0.wireOp",EDGE,"E4");var subQ2=sQuery(id+"F0.wireOp",EDGE,"E3");Q16=makeQuery(id+"F5.opFillet","BLEND_EDGE",EDGE,{"blendedFrom":[makeQuery(id+"F2.boolean.opBoolean","MERGE",EDGE,{"derivedFrom":[makeQuery(id+"F1.opExtrude","SWEPT_EDGE",EDGE,{"disambiguationData":[OSD([subQ2,subQ1])]}),makeQuery(id+"F2.opExtrude","SWEPT_EDGE",EDGE,{"disambiguationData":[OSD([subQ2,subQ1])]})]}),makeQuery(id+"F4.opFillet","BLEND_FACE",FACE,{"disambiguationData":[OSD([subQ0]),TDD([makeQuery(id+"F1.opExtrude","CAP_EDGE",EDGE,{"disambiguationData":[OSD([subQ0])],"isStart":false})]),OD(1.0)]})],"blendedInto":[makeQuery(id+"F4.opFillet","BLEND_FACE",FACE,{"disambiguationData":[OSD([subQ0]),TDD([makeQuery(id+"F1.opExtrude","CAP_EDGE",EDGE,{"disambiguationData":[OSD([subQ0])],"isStart":false})]),OD(1.0)]})]});}
            var Q17;
            {var subQ0=sQuery(id+"F0.wireOp",EDGE,"E2.filletArc");var subQ1=sQuery(id+"F0.wireOp",EDGE,"E5");var subQ2=sQuery(id+"F0.wireOp",EDGE,"E4");var subQ3=sQuery(id+"F0.wireOp",EDGE,"E3");Q17=makeQuery(id+"F5.opFillet","BLEND_EDGE",EDGE,{"blendedFrom":[makeQuery(id+"F2.boolean.opBoolean","MERGE",EDGE,{"derivedFrom":[makeQuery(id+"F1.opExtrude","SWEPT_EDGE",EDGE,{"disambiguationData":[OSD([subQ3,subQ2])]}),makeQuery(id+"F2.opExtrude","SWEPT_EDGE",EDGE,{"disambiguationData":[OSD([subQ3,subQ2])]})]}),makeQuery(id+"F4.opFillet","BLEND_FACE",FACE,{"disambiguationData":[OSD([subQ0,subQ1]),TDD([makeQuery(id+"F3.opFillet","BLEND_EDGE",EDGE,{"blendedFrom":[makeQuery(id+"F1.opExtrude","CAP_EDGE",EDGE,{"disambiguationData":[OSD([subQ1])],"isStart":false}),makeQuery(id+"F2.boolean.opBoolean","MERGE",FACE,{"derivedFrom":[makeQuery(id+"F1.opExtrude","SWEPT_FACE",FACE,{"disambiguationData":[OSD([subQ0])]}),makeQuery(id+"F2.opExtrude","SWEPT_FACE",FACE,{"disambiguationData":[OSD([subQ0])]})]})],"blendedInto":[makeQuery(id+"F2.boolean.opBoolean","MERGE",FACE,{"derivedFrom":[makeQuery(id+"F1.opExtrude","SWEPT_FACE",FACE,{"disambiguationData":[OSD([subQ0])]}),makeQuery(id+"F2.opExtrude","SWEPT_FACE",FACE,{"disambiguationData":[OSD([subQ0])]})]})]})])]})],"blendedInto":[makeQuery(id+"F4.opFillet","BLEND_FACE",FACE,{"disambiguationData":[OSD([subQ0,subQ1]),TDD([makeQuery(id+"F3.opFillet","BLEND_EDGE",EDGE,{"blendedFrom":[makeQuery(id+"F1.opExtrude","CAP_EDGE",EDGE,{"disambiguationData":[OSD([subQ1])],"isStart":false}),makeQuery(id+"F2.boolean.opBoolean","MERGE",FACE,{"derivedFrom":[makeQuery(id+"F1.opExtrude","SWEPT_FACE",FACE,{"disambiguationData":[OSD([subQ0])]}),makeQuery(id+"F2.opExtrude","SWEPT_FACE",FACE,{"disambiguationData":[OSD([subQ0])]})]})],"blendedInto":[makeQuery(id+"F2.boolean.opBoolean","MERGE",FACE,{"derivedFrom":[makeQuery(id+"F1.opExtrude","SWEPT_FACE",FACE,{"disambiguationData":[OSD([subQ0])]}),makeQuery(id+"F2.opExtrude","SWEPT_FACE",FACE,{"disambiguationData":[OSD([subQ0])]})]})]})])]})]});}
            var Q18;
            {var subQ0=sQuery(id+"F0.wireOp",EDGE,"E1");var subQ1=sQuery(id+"F0.wireOp",EDGE,"E5");var subQ2=sQuery(id+"F0.wireOp",EDGE,"E4");var subQ3=sQuery(id+"F0.wireOp",EDGE,"E3");Q18=makeQuery(id+"F5.opFillet","BLEND_EDGE",EDGE,{"blendedFrom":[makeQuery(id+"F2.boolean.opBoolean","MERGE",EDGE,{"derivedFrom":[makeQuery(id+"F1.opExtrude","SWEPT_EDGE",EDGE,{"disambiguationData":[OSD([subQ3,subQ2])]}),makeQuery(id+"F2.opExtrude","SWEPT_EDGE",EDGE,{"disambiguationData":[OSD([subQ3,subQ2])]})]}),makeQuery(id+"F4.opFillet","BLEND_FACE",FACE,{"disambiguationData":[OSD([subQ0,subQ1]),TDD([makeQuery(id+"F3.opFillet","BLEND_EDGE",EDGE,{"blendedFrom":[makeQuery(id+"F1.opExtrude","CAP_EDGE",EDGE,{"disambiguationData":[OSD([subQ1])],"isStart":false}),makeQuery(id+"F2.boolean.opBoolean","MERGE",FACE,{"derivedFrom":[makeQuery(id+"F1.opExtrude","SWEPT_FACE",FACE,{"disambiguationData":[OSD([subQ0])]}),makeQuery(id+"F2.opExtrude","SWEPT_FACE",FACE,{"disambiguationData":[OSD([subQ0])]})]})],"blendedInto":[makeQuery(id+"F2.boolean.opBoolean","MERGE",FACE,{"derivedFrom":[makeQuery(id+"F1.opExtrude","SWEPT_FACE",FACE,{"disambiguationData":[OSD([subQ0])]}),makeQuery(id+"F2.opExtrude","SWEPT_FACE",FACE,{"disambiguationData":[OSD([subQ0])]})]})]})]),OD(0.0)]})],"blendedInto":[makeQuery(id+"F4.opFillet","BLEND_FACE",FACE,{"disambiguationData":[OSD([subQ0,subQ1]),TDD([makeQuery(id+"F3.opFillet","BLEND_EDGE",EDGE,{"blendedFrom":[makeQuery(id+"F1.opExtrude","CAP_EDGE",EDGE,{"disambiguationData":[OSD([subQ1])],"isStart":false}),makeQuery(id+"F2.boolean.opBoolean","MERGE",FACE,{"derivedFrom":[makeQuery(id+"F1.opExtrude","SWEPT_FACE",FACE,{"disambiguationData":[OSD([subQ0])]}),makeQuery(id+"F2.opExtrude","SWEPT_FACE",FACE,{"disambiguationData":[OSD([subQ0])]})]})],"blendedInto":[makeQuery(id+"F2.boolean.opBoolean","MERGE",FACE,{"derivedFrom":[makeQuery(id+"F1.opExtrude","SWEPT_FACE",FACE,{"disambiguationData":[OSD([subQ0])]}),makeQuery(id+"F2.opExtrude","SWEPT_FACE",FACE,{"disambiguationData":[OSD([subQ0])]})]})]})]),OD(0.0)]})]});}
            var Q19;
            {var subQ0=sQuery(id+"F0.wireOp",EDGE,"E4");var subQ1=sQuery(id+"F0.wireOp",EDGE,"E1");Q19=makeQuery(id+"F4.opFillet","BLEND_EDGE",EDGE,{"disambiguationData":[OD(0.0)],"blendedFrom":[makeQuery(id+"F3.opFillet","BLEND_EDGE",EDGE,{"blendedFrom":[makeQuery(id+"F1.opExtrude","CAP_EDGE",EDGE,{"disambiguationData":[OSD([sQuery(id+"F0.wireOp",EDGE,"E5")])],"isStart":false}),makeQuery(id+"F2.boolean.opBoolean","MERGE",FACE,{"derivedFrom":[makeQuery(id+"F1.opExtrude","SWEPT_FACE",FACE,{"disambiguationData":[OSD([subQ1])]}),makeQuery(id+"F2.opExtrude","SWEPT_FACE",FACE,{"disambiguationData":[OSD([subQ1])]})]})],"blendedInto":[makeQuery(id+"F2.boolean.opBoolean","MERGE",FACE,{"derivedFrom":[makeQuery(id+"F1.opExtrude","SWEPT_FACE",FACE,{"disambiguationData":[OSD([subQ1])]}),makeQuery(id+"F2.opExtrude","SWEPT_FACE",FACE,{"disambiguationData":[OSD([subQ1])]})]})]}),makeQuery(id+"F2.boolean.opBoolean","MERGE",FACE,{"derivedFrom":[makeQuery(id+"F1.opExtrude","SWEPT_FACE",FACE,{"disambiguationData":[OSD([subQ0])]}),makeQuery(id+"F2.opExtrude","SWEPT_FACE",FACE,{"disambiguationData":[OSD([subQ0])]})]})],"blendedInto":[makeQuery(id+"F2.boolean.opBoolean","MERGE",FACE,{"derivedFrom":[makeQuery(id+"F1.opExtrude","SWEPT_FACE",FACE,{"disambiguationData":[OSD([subQ0])]}),makeQuery(id+"F2.opExtrude","SWEPT_FACE",FACE,{"disambiguationData":[OSD([subQ0])]})]})]});}
            var Q20;
            {var subQ0=sQuery(id+"F0.wireOp",EDGE,"E4");var subQ1=sQuery(id+"F0.wireOp",EDGE,"E1");Q20=makeQuery(id+"F4.opFillet","BLEND_EDGE",EDGE,{"disambiguationData":[OD(1.0)],"blendedFrom":[makeQuery(id+"F3.opFillet","BLEND_EDGE",EDGE,{"blendedFrom":[makeQuery(id+"F1.opExtrude","CAP_EDGE",EDGE,{"disambiguationData":[OSD([sQuery(id+"F0.wireOp",EDGE,"E5")])],"isStart":false}),makeQuery(id+"F2.boolean.opBoolean","MERGE",FACE,{"derivedFrom":[makeQuery(id+"F1.opExtrude","SWEPT_FACE",FACE,{"disambiguationData":[OSD([subQ1])]}),makeQuery(id+"F2.opExtrude","SWEPT_FACE",FACE,{"disambiguationData":[OSD([subQ1])]})]})],"blendedInto":[makeQuery(id+"F2.boolean.opBoolean","MERGE",FACE,{"derivedFrom":[makeQuery(id+"F1.opExtrude","SWEPT_FACE",FACE,{"disambiguationData":[OSD([subQ1])]}),makeQuery(id+"F2.opExtrude","SWEPT_FACE",FACE,{"disambiguationData":[OSD([subQ1])]})]})]}),makeQuery(id+"F2.boolean.opBoolean","MERGE",FACE,{"derivedFrom":[makeQuery(id+"F1.opExtrude","SWEPT_FACE",FACE,{"disambiguationData":[OSD([subQ0])]}),makeQuery(id+"F2.opExtrude","SWEPT_FACE",FACE,{"disambiguationData":[OSD([subQ0])]})]})],"blendedInto":[makeQuery(id+"F2.boolean.opBoolean","MERGE",FACE,{"derivedFrom":[makeQuery(id+"F1.opExtrude","SWEPT_FACE",FACE,{"disambiguationData":[OSD([subQ0])]}),makeQuery(id+"F2.opExtrude","SWEPT_FACE",FACE,{"disambiguationData":[OSD([subQ0])]})]})]});}
            var Q21;
            {var subQ0=sQuery(id+"F0.wireOp",EDGE,"E4");var subQ1=sQuery(id+"F0.wireOp",EDGE,"E1");Q21=makeQuery(id+"F4.opFillet","BLEND_EDGE",EDGE,{"blendedFrom":[makeQuery(id+"F3.opFillet","BLEND_EDGE",EDGE,{"blendedFrom":[makeQuery(id+"F2.opExtrude","CAP_EDGE",EDGE,{"disambiguationData":[OSD([sQuery(id+"F0.wireOp",EDGE,"E5")])],"isStart":false}),makeQuery(id+"F2.boolean.opBoolean","MERGE",FACE,{"derivedFrom":[makeQuery(id+"F1.opExtrude","SWEPT_FACE",FACE,{"disambiguationData":[OSD([subQ1])]}),makeQuery(id+"F2.opExtrude","SWEPT_FACE",FACE,{"disambiguationData":[OSD([subQ1])]})]})],"blendedInto":[makeQuery(id+"F2.boolean.opBoolean","MERGE",FACE,{"derivedFrom":[makeQuery(id+"F1.opExtrude","SWEPT_FACE",FACE,{"disambiguationData":[OSD([subQ1])]}),makeQuery(id+"F2.opExtrude","SWEPT_FACE",FACE,{"disambiguationData":[OSD([subQ1])]})]})]}),makeQuery(id+"F2.boolean.opBoolean","MERGE",FACE,{"derivedFrom":[makeQuery(id+"F1.opExtrude","SWEPT_FACE",FACE,{"disambiguationData":[OSD([subQ0])]}),makeQuery(id+"F2.opExtrude","SWEPT_FACE",FACE,{"disambiguationData":[OSD([subQ0])]})]})],"blendedInto":[makeQuery(id+"F2.boolean.opBoolean","MERGE",FACE,{"derivedFrom":[makeQuery(id+"F1.opExtrude","SWEPT_FACE",FACE,{"disambiguationData":[OSD([subQ0])]}),makeQuery(id+"F2.opExtrude","SWEPT_FACE",FACE,{"disambiguationData":[OSD([subQ0])]})]})]});}
            var Q22;
            {var subQ0=sQuery(id+"F0.wireOp",EDGE,"E4");var subQ1=sQuery(id+"F0.wireOp",EDGE,"E5");var subQ2=sQuery(id+"F0.wireOp",EDGE,"E1");Q22=makeQuery(id+"F4.opFillet","BLEND_EDGE",EDGE,{"blendedFrom":[makeQuery(id+"F2.boolean.opBoolean","MERGE",EDGE,{"derivedFrom":[makeQuery(id+"F1.opExtrude","SWEPT_EDGE",EDGE,{"disambiguationData":[OSD([subQ2,subQ1])]}),makeQuery(id+"F2.opExtrude","SWEPT_EDGE",EDGE,{"disambiguationData":[OSD([subQ2,subQ1])]})]}),makeQuery(id+"F2.boolean.opBoolean","MERGE",FACE,{"derivedFrom":[makeQuery(id+"F1.opExtrude","SWEPT_FACE",FACE,{"disambiguationData":[OSD([subQ0])]}),makeQuery(id+"F2.opExtrude","SWEPT_FACE",FACE,{"disambiguationData":[OSD([subQ0])]})]})],"blendedInto":[makeQuery(id+"F2.boolean.opBoolean","MERGE",FACE,{"derivedFrom":[makeQuery(id+"F1.opExtrude","SWEPT_FACE",FACE,{"disambiguationData":[OSD([subQ0])]}),makeQuery(id+"F2.opExtrude","SWEPT_FACE",FACE,{"disambiguationData":[OSD([subQ0])]})]})]});}
            var Q23;
            {var subQ0=sQuery(id+"F0.wireOp",EDGE,"E4");var subQ1=sQuery(id+"F0.wireOp",EDGE,"E2.filletArc");Q23=makeQuery(id+"F4.opFillet","BLEND_EDGE",EDGE,{"blendedFrom":[makeQuery(id+"F3.opFillet","BLEND_EDGE",EDGE,{"blendedFrom":[makeQuery(id+"F2.opExtrude","CAP_EDGE",EDGE,{"disambiguationData":[OSD([sQuery(id+"F0.wireOp",EDGE,"E5")])],"isStart":false}),makeQuery(id+"F2.boolean.opBoolean","MERGE",FACE,{"derivedFrom":[makeQuery(id+"F1.opExtrude","SWEPT_FACE",FACE,{"disambiguationData":[OSD([subQ1])]}),makeQuery(id+"F2.opExtrude","SWEPT_FACE",FACE,{"disambiguationData":[OSD([subQ1])]})]})],"blendedInto":[makeQuery(id+"F2.boolean.opBoolean","MERGE",FACE,{"derivedFrom":[makeQuery(id+"F1.opExtrude","SWEPT_FACE",FACE,{"disambiguationData":[OSD([subQ1])]}),makeQuery(id+"F2.opExtrude","SWEPT_FACE",FACE,{"disambiguationData":[OSD([subQ1])]})]})]}),makeQuery(id+"F2.boolean.opBoolean","MERGE",FACE,{"derivedFrom":[makeQuery(id+"F1.opExtrude","SWEPT_FACE",FACE,{"disambiguationData":[OSD([subQ0])]}),makeQuery(id+"F2.opExtrude","SWEPT_FACE",FACE,{"disambiguationData":[OSD([subQ0])]})]})],"blendedInto":[makeQuery(id+"F2.boolean.opBoolean","MERGE",FACE,{"derivedFrom":[makeQuery(id+"F1.opExtrude","SWEPT_FACE",FACE,{"disambiguationData":[OSD([subQ0])]}),makeQuery(id+"F2.opExtrude","SWEPT_FACE",FACE,{"disambiguationData":[OSD([subQ0])]})]})]});}
            var Q24;
            {var subQ0=sQuery(id+"F0.wireOp",EDGE,"E2.filletArc");var subQ1=sQuery(id+"F0.wireOp",EDGE,"E5");var subQ2=sQuery(id+"F0.wireOp",EDGE,"E4");var subQ3=sQuery(id+"F0.wireOp",EDGE,"E3");Q24=makeQuery(id+"F5.opFillet","BLEND_EDGE",EDGE,{"blendedFrom":[makeQuery(id+"F2.boolean.opBoolean","MERGE",EDGE,{"derivedFrom":[makeQuery(id+"F1.opExtrude","SWEPT_EDGE",EDGE,{"disambiguationData":[OSD([subQ3,subQ2])]}),makeQuery(id+"F2.opExtrude","SWEPT_EDGE",EDGE,{"disambiguationData":[OSD([subQ3,subQ2])]})]}),makeQuery(id+"F4.opFillet","BLEND_FACE",FACE,{"disambiguationData":[OSD([subQ0,subQ1]),TDD([makeQuery(id+"F3.opFillet","BLEND_EDGE",EDGE,{"blendedFrom":[makeQuery(id+"F2.opExtrude","CAP_EDGE",EDGE,{"disambiguationData":[OSD([subQ1])],"isStart":false}),makeQuery(id+"F2.boolean.opBoolean","MERGE",FACE,{"derivedFrom":[makeQuery(id+"F1.opExtrude","SWEPT_FACE",FACE,{"disambiguationData":[OSD([subQ0])]}),makeQuery(id+"F2.opExtrude","SWEPT_FACE",FACE,{"disambiguationData":[OSD([subQ0])]})]})],"blendedInto":[makeQuery(id+"F2.boolean.opBoolean","MERGE",FACE,{"derivedFrom":[makeQuery(id+"F1.opExtrude","SWEPT_FACE",FACE,{"disambiguationData":[OSD([subQ0])]}),makeQuery(id+"F2.opExtrude","SWEPT_FACE",FACE,{"disambiguationData":[OSD([subQ0])]})]})]})]),OD(0.0)]})],"blendedInto":[makeQuery(id+"F4.opFillet","BLEND_FACE",FACE,{"disambiguationData":[OSD([subQ0,subQ1]),TDD([makeQuery(id+"F3.opFillet","BLEND_EDGE",EDGE,{"blendedFrom":[makeQuery(id+"F2.opExtrude","CAP_EDGE",EDGE,{"disambiguationData":[OSD([subQ1])],"isStart":false}),makeQuery(id+"F2.boolean.opBoolean","MERGE",FACE,{"derivedFrom":[makeQuery(id+"F1.opExtrude","SWEPT_FACE",FACE,{"disambiguationData":[OSD([subQ0])]}),makeQuery(id+"F2.opExtrude","SWEPT_FACE",FACE,{"disambiguationData":[OSD([subQ0])]})]})],"blendedInto":[makeQuery(id+"F2.boolean.opBoolean","MERGE",FACE,{"derivedFrom":[makeQuery(id+"F1.opExtrude","SWEPT_FACE",FACE,{"disambiguationData":[OSD([subQ0])]}),makeQuery(id+"F2.opExtrude","SWEPT_FACE",FACE,{"disambiguationData":[OSD([subQ0])]})]})]})]),OD(0.0)]})]});}
            var Q25;
            {var subQ0=sQuery(id+"F0.wireOp",EDGE,"E2.filletArc");var subQ1=sQuery(id+"F0.wireOp",EDGE,"E5");var subQ2=sQuery(id+"F0.wireOp",EDGE,"E4");var subQ3=sQuery(id+"F0.wireOp",EDGE,"E3");Q25=makeQuery(id+"F5.opFillet","BLEND_EDGE",EDGE,{"blendedFrom":[makeQuery(id+"F2.boolean.opBoolean","MERGE",EDGE,{"derivedFrom":[makeQuery(id+"F1.opExtrude","SWEPT_EDGE",EDGE,{"disambiguationData":[OSD([subQ3,subQ2])]}),makeQuery(id+"F2.opExtrude","SWEPT_EDGE",EDGE,{"disambiguationData":[OSD([subQ3,subQ2])]})]}),makeQuery(id+"F4.opFillet","BLEND_FACE",FACE,{"disambiguationData":[OSD([subQ0,subQ1]),TDD([makeQuery(id+"F3.opFillet","BLEND_EDGE",EDGE,{"blendedFrom":[makeQuery(id+"F2.opExtrude","CAP_EDGE",EDGE,{"disambiguationData":[OSD([subQ1])],"isStart":false}),makeQuery(id+"F2.boolean.opBoolean","MERGE",FACE,{"derivedFrom":[makeQuery(id+"F1.opExtrude","SWEPT_FACE",FACE,{"disambiguationData":[OSD([subQ0])]}),makeQuery(id+"F2.opExtrude","SWEPT_FACE",FACE,{"disambiguationData":[OSD([subQ0])]})]})],"blendedInto":[makeQuery(id+"F2.boolean.opBoolean","MERGE",FACE,{"derivedFrom":[makeQuery(id+"F1.opExtrude","SWEPT_FACE",FACE,{"disambiguationData":[OSD([subQ0])]}),makeQuery(id+"F2.opExtrude","SWEPT_FACE",FACE,{"disambiguationData":[OSD([subQ0])]})]})]})]),OD(1.0)]})],"blendedInto":[makeQuery(id+"F4.opFillet","BLEND_FACE",FACE,{"disambiguationData":[OSD([subQ0,subQ1]),TDD([makeQuery(id+"F3.opFillet","BLEND_EDGE",EDGE,{"blendedFrom":[makeQuery(id+"F2.opExtrude","CAP_EDGE",EDGE,{"disambiguationData":[OSD([subQ1])],"isStart":false}),makeQuery(id+"F2.boolean.opBoolean","MERGE",FACE,{"derivedFrom":[makeQuery(id+"F1.opExtrude","SWEPT_FACE",FACE,{"disambiguationData":[OSD([subQ0])]}),makeQuery(id+"F2.opExtrude","SWEPT_FACE",FACE,{"disambiguationData":[OSD([subQ0])]})]})],"blendedInto":[makeQuery(id+"F2.boolean.opBoolean","MERGE",FACE,{"derivedFrom":[makeQuery(id+"F1.opExtrude","SWEPT_FACE",FACE,{"disambiguationData":[OSD([subQ0])]}),makeQuery(id+"F2.opExtrude","SWEPT_FACE",FACE,{"disambiguationData":[OSD([subQ0])]})]})]})]),OD(1.0)]})]});}
            var Q26;
            {var subQ0=sQuery(id+"F0.wireOp",EDGE,"E2.filletArc");var subQ1=sQuery(id+"F0.wireOp",EDGE,"E4");var subQ2=sQuery(id+"F0.wireOp",EDGE,"E3");Q26=makeQuery(id+"F5.opFillet","BLEND_EDGE",EDGE,{"blendedFrom":[makeQuery(id+"F2.boolean.opBoolean","MERGE",EDGE,{"derivedFrom":[makeQuery(id+"F1.opExtrude","SWEPT_EDGE",EDGE,{"disambiguationData":[OSD([subQ2,subQ1])]}),makeQuery(id+"F2.opExtrude","SWEPT_EDGE",EDGE,{"disambiguationData":[OSD([subQ2,subQ1])]})]}),makeQuery(id+"F4.opFillet","BLEND_FACE",FACE,{"disambiguationData":[OSD([subQ0]),TDD([makeQuery(id+"F2.opExtrude","CAP_EDGE",EDGE,{"disambiguationData":[OSD([subQ0])],"isStart":false})])]})],"blendedInto":[makeQuery(id+"F4.opFillet","BLEND_FACE",FACE,{"disambiguationData":[OSD([subQ0]),TDD([makeQuery(id+"F2.opExtrude","CAP_EDGE",EDGE,{"disambiguationData":[OSD([subQ0])],"isStart":false})])]})]});}
            var Q27;
            {var subQ0=sQuery(id+"F0.wireOp",EDGE,"E7.MirrorCS");var subQ1=sQuery(id+"F0.wireOp",EDGE,"E3");Q27=makeQuery(id+"F4.opFillet","BLEND_EDGE",EDGE,{"blendedFrom":[makeQuery(id+"F2.opExtrude","CAP_EDGE",EDGE,{"disambiguationData":[OSD([sQuery(id+"F0.wireOp",EDGE,"E2.filletArc")])],"isStart":false}),makeQuery(id+"F2.boolean.opBoolean","MERGE",FACE,{"derivedFrom":[makeQuery(id+"F1.opExtrude","SWEPT_FACE",FACE,{"disambiguationData":[OSD([subQ1,subQ0])]}),makeQuery(id+"F2.opExtrude","SWEPT_FACE",FACE,{"disambiguationData":[OSD([subQ1,subQ0])]})]})],"blendedInto":[makeQuery(id+"F2.boolean.opBoolean","MERGE",FACE,{"derivedFrom":[makeQuery(id+"F1.opExtrude","SWEPT_FACE",FACE,{"disambiguationData":[OSD([subQ1,subQ0])]}),makeQuery(id+"F2.opExtrude","SWEPT_FACE",FACE,{"disambiguationData":[OSD([subQ1,subQ0])]})]})]});}
            fillet(context, id + "F6", {"entities" : qUnion([Q0, Q1, Q2, Q3, Q4, Q5, Q6, Q7, Q8, Q9, Q10, Q11, Q12, Q13, Q14, Q15, Q16, Q17, Q18, Q19, Q20, Q21, Q22, Q23, Q24, Q25, Q26, Q27]), "radius" : 0.13 * mm, "tangentPropagation" : true, "allowEdgeOverflow" : false});
        }
        {
            var Q0;
            {var subQ0=sQuery(id+"F0.wireOp",EDGE,"E7.MirrorCS");var subQ1=sQuery(id+"F0.wireOp",EDGE,"E3");Q0=makeQuery(id+"F2.boolean.opBoolean","MERGE",FACE,{"derivedFrom":[makeQuery(id+"F1.opExtrude","SWEPT_FACE",FACE,{"disambiguationData":[OSD([subQ1,subQ0])]}),makeQuery(id+"F2.opExtrude","SWEPT_FACE",FACE,{"disambiguationData":[OSD([subQ1,subQ0])]})]});}
            var sketch = newSketch(context, id + "F7", { "sketchPlane" : qUnion([Q0])});
            skLineSegment(sketch, "E13.bottom", {"start": v(1.9, 6.66) * mm, "end": v(-1.9, 6.66) * mm});
            skLineSegment(sketch, "E13.top", {"start": v(1.9, 4.8) * mm, "end": v(-1.9, 4.8) * mm});
            skLineSegment(sketch, "E13.left", {"start": v(1.9, 6.66) * mm, "end": v(1.9, 4.8) * mm});
            skLineSegment(sketch, "E13.right", {"start": v(-1.9, 6.66) * mm, "end": v(-1.9, 4.8) * mm});
            skPoint(sketch, "E13.middle", {"position": v(0, 5.73) * mm});
            skLineSegment(sketch, "E14", {"start": v(-6.09, 0) * mm, "end": v(7.1, 0) * mm});
            skLineSegment(sketch, "E15.MirrorCS", {"start": v(1.9, -4.8) * mm, "end": v(-1.9, -4.8) * mm});
            skLineSegment(sketch, "E16.MirrorCS", {"start": v(1.9, -6.66) * mm, "end": v(1.9, -4.8) * mm});
            skLineSegment(sketch, "E17.MirrorCS", {"start": v(1.9, -6.66) * mm, "end": v(-1.9, -6.66) * mm});
            skLineSegment(sketch, "E18.MirrorCS", {"start": v(-1.9, -6.66) * mm, "end": v(-1.9, -4.8) * mm});
            skCircle(sketch, "E19", {"center": v(0, 0) * mm, "radius": 0.65 * mm});
            skSolve(sketch);
        }
        {
            var Q0;
            Q0=makeQuery(id+"F7.imprint","IMPRINT",FACE,{"disambiguationData":[TD([[makeQuery(id+"F7.imprint","IMPRINT",EDGE,{"derivedFrom":sQuery(id+"F7.wireOp",EDGE,"E13.bottom")}),1.0]])]});
            var Q1;
            Q1=makeQuery(id+"F7.imprint","IMPRINT",FACE,{"disambiguationData":[TD([[makeQuery(id+"F7.imprint","IMPRINT",EDGE,{"derivedFrom":sQuery(id+"F7.wireOp",EDGE,"E15.MirrorCS")}),1.0]])]});
            extrude(context, id + "F8", {"entities" : qUnion([Q0, Q1]), "operationType" : NewBodyOperationType.REMOVE, "oppositeDirection" : true, "depth" : 0.25 * mm});
        }
        {
            var Q0;
            Q0=makeQuery(id+"F8.boolean.opBoolean","COPY",EDGE,{"derivedFrom":makeQuery(id+"F8.opExtrude","SWEPT_EDGE",EDGE,{"disambiguationData":[OSD([sQuery(id+"F7.wireOp",EDGE,"E13.bottom"),sQuery(id+"F7.wireOp",EDGE,"E13.right")])]})});
            var Q1;
            Q1=makeQuery(id+"F8.boolean.opBoolean","COPY",EDGE,{"derivedFrom":makeQuery(id+"F8.opExtrude","SWEPT_EDGE",EDGE,{"disambiguationData":[OSD([sQuery(id+"F7.wireOp",EDGE,"E13.top"),sQuery(id+"F7.wireOp",EDGE,"E13.right")])]})});
            var Q2;
            Q2=makeQuery(id+"F8.boolean.opBoolean","COPY",EDGE,{"derivedFrom":makeQuery(id+"F8.opExtrude","SWEPT_EDGE",EDGE,{"disambiguationData":[OSD([sQuery(id+"F7.wireOp",EDGE,"E15.MirrorCS"),sQuery(id+"F7.wireOp",EDGE,"E18.MirrorCS")])]})});
            var Q3;
            Q3=makeQuery(id+"F8.boolean.opBoolean","COPY",EDGE,{"derivedFrom":makeQuery(id+"F8.opExtrude","SWEPT_EDGE",EDGE,{"disambiguationData":[OSD([sQuery(id+"F7.wireOp",EDGE,"E17.MirrorCS"),sQuery(id+"F7.wireOp",EDGE,"E18.MirrorCS")])]})});
            var Q4;
            Q4=makeQuery(id+"F8.boolean.opBoolean","COPY",EDGE,{"derivedFrom":makeQuery(id+"F8.opExtrude","CAP_EDGE",EDGE,{"disambiguationData":[OSD([sQuery(id+"F7.wireOp",EDGE,"E13.bottom")])],"isStart":false})});
            var Q5;
            Q5=makeQuery(id+"F8.boolean.opBoolean","COPY",EDGE,{"derivedFrom":makeQuery(id+"F8.opExtrude","CAP_EDGE",EDGE,{"disambiguationData":[OSD([sQuery(id+"F7.wireOp",EDGE,"E13.top")])],"isStart":false})});
            var Q6;
            Q6=makeQuery(id+"F8.boolean.opBoolean","COPY",EDGE,{"derivedFrom":makeQuery(id+"F8.opExtrude","CAP_EDGE",EDGE,{"disambiguationData":[OSD([sQuery(id+"F7.wireOp",EDGE,"E13.left")])],"isStart":false})});
            var Q7;
            Q7=makeQuery(id+"F8.boolean.opBoolean","COPY",EDGE,{"derivedFrom":makeQuery(id+"F8.opExtrude","CAP_EDGE",EDGE,{"disambiguationData":[OSD([sQuery(id+"F7.wireOp",EDGE,"E17.MirrorCS")])],"isStart":false})});
            var Q8;
            Q8=makeQuery(id+"F8.boolean.opBoolean","COPY",EDGE,{"derivedFrom":makeQuery(id+"F8.opExtrude","CAP_EDGE",EDGE,{"disambiguationData":[OSD([sQuery(id+"F7.wireOp",EDGE,"E16.MirrorCS")])],"isStart":false})});
            var Q9;
            Q9=makeQuery(id+"F8.boolean.opBoolean","COPY",EDGE,{"derivedFrom":makeQuery(id+"F8.opExtrude","CAP_EDGE",EDGE,{"disambiguationData":[OSD([sQuery(id+"F7.wireOp",EDGE,"E15.MirrorCS")])],"isStart":false})});
            fillet(context, id + "F9", {"entities" : qUnion([Q0, Q1, Q2, Q3, Q4, Q5, Q6, Q7, Q8, Q9]), "radius" : 0.76 * mm, "tangentPropagation" : true, "allowEdgeOverflow" : false});
        }
        {
            var Q0;
            {var subQ0=sQuery(id+"F7.wireOp",EDGE,"E19");var subQ1=sQuery(id+"F7.wireOp",EDGE,"E14");var subQ2=makeQuery(id+"F7.imprint","INTERSECT",VERTEX,{"disambiguationData":[OD(0.0)],"derivedFrom":[subQ1,subQ0]});Q0=makeQuery(id+"F7.imprint","IMPRINT",FACE,{"disambiguationData":[TD([[makeQuery(id+"F7.imprint","IMPRINT",EDGE,{"disambiguationData":[TD([[subQ2,-1.0]])],"derivedFrom":subQ1}),1.0]])]});}
            var Q1;
            {var subQ0=sQuery(id+"F7.wireOp",EDGE,"E19");var subQ1=sQuery(id+"F7.wireOp",EDGE,"E14");var subQ2=makeQuery(id+"F7.imprint","INTERSECT",VERTEX,{"disambiguationData":[OD(0.0)],"derivedFrom":[subQ1,subQ0]});Q1=makeQuery(id+"F7.imprint","IMPRINT",FACE,{"disambiguationData":[TD([[makeQuery(id+"F7.imprint","IMPRINT",EDGE,{"disambiguationData":[TD([[subQ2,-1.0]])],"derivedFrom":subQ1}),-1.0]])]});}
            extrude(context, id + "F10", {"entities" : qUnion([Q0, Q1]), "operationType" : NewBodyOperationType.ADD, "depth" : 0.25 * mm});
        }
        {
            var Q0;
            Q0=makeQuery(id+"F10.opExtrude","CAP_EDGE",EDGE,{"disambiguationData":[OSD([sQuery(id+"F7.wireOp",EDGE,"E19")])],"isStart":false});
            fillet(context, id + "F11", {"entities" : qUnion([Q0]), "radius" : 0.25 * mm, "tangentPropagation" : true, "allowEdgeOverflow" : false});
        }
    });
